SOLIDWORKS PART (.sldprt)
format: sldprt  version: not decoded by parser v0  size: 606,208 bytes
history: native  units: mm
features: sketch x494, extrude x1 + 10 further entries (+10 scaffold rows collapsed; 88 parser-record rows omitted)
feature tree (603):
  "Annotations"  RD1=95.25mm RD2=113.058536mm RD3=120.65mm RD4=130.291107mm RD6=10.3124mm RD5=12.7mm RD7=12.7mm RD8=12.7mm RD9=12.7mm RD10=12.7mm RD11=10.3124mm RD12=10.3124mm RD13=14.199032mm
  scaffold x10  (default folders/planes/origin — collapsed)
  sketch  "Sketch2"  dims[c1.D1=6.35mm c1.D2=6.35mm c1.D3=3.175mm c1.D4=3.175mm c2.D1=2.54mm c2.D2=2.54mm c2.D3=1.27mm c2.D4=1.27mm c3.D2=2.54mm c3.D3=2.54mm c3.D1=2.54mm c3.D5=2.54mm c3.D6=2.54mm c4.D1=2.54mm c4.D7=2.54mm c5.D1=2.54mm c5.D5=2.54mm c5.D2=2.54mm c5.D3=2.54mm c5.D6=~1.365496mm c6.D1=304.8mm c7.D1=~44.215175deg c8.D1=~862.162868mm c9.D1=~23.628086mm c10.D1=~757.905383mm c11.D1=~6.290207mm c11.D6=~14.447018mm c12.D1=6.35mm c12.D2=6.35mm c13.D1=3.048mm c13.D2=3.048mm c14.D1=1.524mm c14.D2=1.524mm c15.D1=6.35mm c15.D2=6.35mm c16.D1=10.16mm c16.D2=10.16mm c16.D3=7.62mm c16.D4=7.62mm c16.D5=8.89mm c16.D6=8.89mm c17.D1=8.89mm c17.D2=6.35mm c17.D3=6.35mm c18.D1=2.54mm c18.D2=2.54mm c19.D1=2.54mm c19.D2=2.54mm c19.D4=1.27mm c19.D5=1.27mm c19.D3=4.572mm c20.D5=4.572mm c20.D3=4.572mm c21.D5=4.572mm c21.D3=2.54mm c22.D5=2.54mm c22.D6=2.54mm c22.D3=1.27mm c23.D5=16.51mm c23.D6=1.27mm c23.D7=1.27mm c23.D8=10.16mm c23.D9=2.54mm c24.D8=5.08mm c24.D9=5.08mm c24.D5=5.08mm c24.D6=5.08mm c25.D8=1.905mm c25.D9=1.905mm c25.D6=1.905mm c26.D8=1.905mm c26.D6=5.08mm c27.D8=1.905mm c27.D9=1.905mm]
  extrude  "Extrude3"  Depth=6.35mm RestraintType=1
  sketch  "Value"
  sketch  "cosRestraintComp:1"
  sketch  "cosRestraintComp:2"
  sketch  "cosRestraintComp:3"
  sketch  "cosRestraintComp:4"
  sketch  "cosRestraintComp:5"
  sketch  "cosRestraintComp:6"
  sketch  "Unit"
  sketch  "AnalysisType"
  sketch  "MeshType"
  sketch  "cosRestraintCompCheck1"
  sketch  "cosRestraintCompCheck2"
  sketch  "cosRestraintCompCheck3"
  sketch  "cosRestraintCompCheck4"
  sketch  "cosRestraintCompCheck5"
  sketch  "cosRestraintCompCheck6"
  sketch  "cosRestraintRefPlaneSet"
  sketch  "cosRestraintRefPlaneOrigin1"
  sketch  "cosRestraintRefPlaneOrigin2"
  sketch  "cosRestraintRefPlaneOrigin3"
  sketch  "cosRestraintRefPlaneXDir1"
  sketch  "cosRestraintRefPlaneXDir2"
  sketch  "cosRestraintRefPlaneXDir3"
  sketch  "cosRestraintRefPlaneNormal1"
  sketch  "cosRestraintRefPlaneNormal2"
  sketch  "cosRestraintRefPlaneNormal3"
  sketch  "cosRestraintCoordSystemType"
  sketch  "cosRestraintFaceTypeMask"  dims[cosFMVItemName=0.0deg cosLBCSymbolColor=0.0deg]
  sketch  "cosLBCState"
  sketch  "RestraintType"
  sketch  "Value"
  sketch  "cosRestraintComp:1"
  sketch  "cosRestraintComp:2"
  sketch  "cosRestraintComp:3"
  sketch  "cosRestraintComp:4"
  sketch  "cosRestraintComp:5"
  sketch  "cosRestraintComp:6"
  sketch  "Unit"
  sketch  "AnalysisType"
  sketch  "MeshType"
  sketch  "cosRestraintCompCheck1"
  sketch  "cosRestraintCompCheck2"
  sketch  "cosRestraintCompCheck3"
  sketch  "cosRestraintCompCheck4"
  sketch  "cosRestraintCompCheck5"
  sketch  "cosRestraintCompCheck6"
  sketch  "cosRestraintRefPlaneSet"
  sketch  "cosRestraintRefPlaneOrigin1"
  sketch  "cosRestraintRefPlaneOrigin2"
  sketch  "cosRestraintRefPlaneOrigin3"
  sketch  "cosRestraintRefPlaneXDir1"
  sketch  "cosRestraintRefPlaneXDir2"
  sketch  "cosRestraintRefPlaneXDir3"
  sketch  "cosRestraintRefPlaneNormal1"
  sketch  "cosRestraintRefPlaneNormal2"
  sketch  "cosRestraintRefPlaneNormal3"  dims[cosRestraintRefPlaneName=0.0deg]
  sketch  "cosRestraintCoordSystemType"
  sketch  "cosRestraintFaceTypeMask"  dims[cosFMVItemName=0.0deg cosLBCSymbolColor=0.0deg]
  sketch  "cosLBCState"
  "freq:Restraint-2"
  sketch  "RestraintType"
  sketch  "Value"
  sketch  "cosRestraintComp:1"
  sketch  "cosRestraintComp:2"
  sketch  "cosRestraintComp:3"
  sketch  "cosRestraintComp:4"
  sketch  "cosRestraintComp:5"
  sketch  "cosRestraintComp:6"
  sketch  "Unit"
  sketch  "AnalysisType"
  sketch  "MeshType"
  sketch  "cosRestraintCompCheck1"
  sketch  "cosRestraintCompCheck2"
  sketch  "cosRestraintCompCheck3"
  sketch  "cosRestraintCompCheck4"
  sketch  "cosRestraintCompCheck5"
  sketch  "cosRestraintCompCheck6"
  sketch  "cosRestraintRefPlaneSet"
  sketch  "cosRestraintRefPlaneOrigin1"
  sketch  "cosRestraintRefPlaneOrigin2"
  sketch  "cosRestraintRefPlaneOrigin3"
  sketch  "cosRestraintRefPlaneXDir1"
  sketch  "cosRestraintRefPlaneXDir2"
  sketch  "cosRestraintRefPlaneXDir3"
  sketch  "cosRestraintRefPlaneNormal1"
  sketch  "cosRestraintRefPlaneNormal2"
  sketch  "cosRestraintRefPlaneNormal3"  dims[cosRestraintRefPlaneName=0.0deg]
  sketch  "cosRestraintCoordSystemType"
  sketch  "cosRestraintFaceTypeMask"  dims[cosFMVItemName=0.0deg cosLBCSymbolColor=0.0deg]
  sketch  "cosLBCState"
  "freq:Force-1"
  sketch  "cosForceComp:1"
  sketch  "cosForceComp:2"
  sketch  "cosForceComp:3"
  sketch  "cosForceComp:4"
  sketch  "cosForceComp:5"
  sketch  "cosForceComp:6"
  sketch  "cosForceTorqueNF"
  sketch  "cosForceCompCheck1"
  sketch  "cosForceCompCheck2"
  sketch  "cosForceCompCheck3"
  sketch  "cosForceCompCheck4"
  sketch  "cosForceCompCheck5"
  sketch  "cosForceCompCheck6"
  sketch  "Unit"
  sketch  "AnalysisType"
  sketch  "MeshType"
  sketch  "cosForceRefPlaneSet"
  sketch  "cosForceRefPlaneOrigin1"
  sketch  "cosForceRefPlaneOrigin2"
  sketch  "cosForceRefPlaneOrigin3"
  sketch  "cosForceRefPlaneXDir1"
  sketch  "cosForceRefPlaneXDir2"
  sketch  "cosForceRefPlaneXDir3"
  sketch  "cosForceRefPlaneNormal1"
  sketch  "cosForceRefPlaneNormal2"
  sketch  "cosForceRefPlaneNormal3"  dims[cosForceRefPlaneName=0.0deg]
  sketch  "cosForceCoordSystemType"
  sketch  "cosForceType"  dims[cosFMVItemName=0.0deg]
  sketch  "cosDistributionType"  dims[cosDistributionCoordSysName=0.0deg]
  sketch  "cosDistributionCoef1"
  sketch  "cosDistributionCoef2"
  sketch  "cosDistributionCoef3"
  sketch  "cosDistributionCoef4"
  sketch  "cosDistributionCoef5"
  sketch  "cosDistributionCoef6"  dims[cosLBCSymbolColor=0.0deg]
  sketch  "cosLBCState"  dims[cosForce7=0.0]
  sketch  "cosForceComp:1"
  sketch  "cosForceComp:2"
  sketch  "cosForceComp:3"
  sketch  "cosForceComp:4"
  sketch  "cosForceComp:5"
  sketch  "cosForceComp:6"
  sketch  "cosForceTorqueNF"
  sketch  "cosForceCompCheck1"
  sketch  "cosForceCompCheck2"
  sketch  "cosForceCompCheck3"
  sketch  "cosForceCompCheck4"
  sketch  "cosForceCompCheck5"
  sketch  "cosForceCompCheck6"
  sketch  "Unit"
  sketch  "AnalysisType"
  sketch  "MeshType"
  sketch  "cosForceRefPlaneSet"
  sketch  "cosForceRefPlaneOrigin1"
  sketch  "cosForceRefPlaneOrigin2"
  sketch  "cosForceRefPlaneOrigin3"
  sketch  "cosForceRefPlaneXDir1"
  sketch  "cosForceRefPlaneXDir2"
  sketch  "cosForceRefPlaneXDir3"
  sketch  "cosForceRefPlaneNormal1"
  sketch  "cosForceRefPlaneNormal2"
  sketch  "cosForceRefPlaneNormal3"  dims[cosForceRefPlaneName=0.0deg]
  sketch  "cosForceCoordSystemType"
  sketch  "cosForceType"  dims[cosFMVItemName=0.0deg]
  sketch  "cosDistributionType"  dims[cosDistributionCoordSysName=0.0deg]
  sketch  "cosDistributionCoef1"
  sketch  "cosDistributionCoef2"
  sketch  "cosDistributionCoef3"
  sketch  "cosDistributionCoef4"
  sketch  "cosDistributionCoef5"
  sketch  "cosDistributionCoef6"  dims[cosLBCSymbolColor=0.0deg]
  sketch  "cosLBCState"
  "freq:Force-2"
  sketch  "cosForceComp:1"
  sketch  "cosForceComp:2"
  sketch  "cosForceComp:3"
  sketch  "cosForceComp:4"
  sketch  "cosForceComp:5"
  sketch  "cosForceComp:6"
  sketch  "cosForceTorqueNF"
  sketch  "cosForceCompCheck1"
  sketch  "cosForceCompCheck2"
  sketch  "cosForceCompCheck3"
  sketch  "cosForceCompCheck4"
  sketch  "cosForceCompCheck5"
  sketch  "cosForceCompCheck6"
  sketch  "Unit"
  sketch  "AnalysisType"
  sketch  "MeshType"
  sketch  "cosForceRefPlaneSet"
  sketch  "cosForceRefPlaneOrigin1"
  sketch  "cosForceRefPlaneOrigin2"
  sketch  "cosForceRefPlaneOrigin3"
  sketch  "cosForceRefPlaneXDir1"
  sketch  "cosForceRefPlaneXDir2"
  sketch  "cosForceRefPlaneXDir3"
  sketch  "cosForceRefPlaneNormal1"
  sketch  "cosForceRefPlaneNormal2"
  sketch  "cosForceRefPlaneNormal3"  dims[cosForceRefPlaneName=0.0deg]
  sketch  "cosForceCoordSystemType"
  sketch  "cosForceType"  dims[cosFMVItemName=0.0deg]
  sketch  "cosDistributionType"  dims[cosDistributionCoordSysName=0.0deg]
  sketch  "cosDistributionCoef1"
  sketch  "cosDistributionCoef2"
  sketch  "cosDistributionCoef3"
  sketch  "cosDistributionCoef4"
  sketch  "cosDistributionCoef5"
  sketch  "cosDistributionCoef6"  dims[cosLBCSymbolColor=0.0deg]
  sketch  "cosLBCState"
  "static:Restraint-3"
  sketch  "RestraintType"
  sketch  "Value"
  sketch  "cosRestraintComp:1"
  sketch  "cosRestraintComp:2"
  sketch  "cosRestraintComp:3"
  sketch  "cosRestraintComp:4"
  sketch  "cosRestraintComp:5"
  sketch  "cosRestraintComp:6"
  sketch  "Unit"
  sketch  "AnalysisType"
  sketch  "MeshType"
  sketch  "cosRestraintCompCheck1"
  sketch  "cosRestraintCompCheck2"
  sketch  "cosRestraintCompCheck3"
  sketch  "cosRestraintCompCheck4"
  sketch  "cosRestraintCompCheck5"
  sketch  "cosRestraintCompCheck6"
  sketch  "cosRestraintRefPlaneSet"
  sketch  "cosRestraintRefPlaneOrigin1"
  sketch  "cosRestraintRefPlaneOrigin2"
  sketch  "cosRestraintRefPlaneOrigin3"
  sketch  "cosRestraintRefPlaneXDir1"
  sketch  "cosRestraintRefPlaneXDir2"
  sketch  "cosRestraintRefPlaneXDir3"
  sketch  "cosRestraintRefPlaneNormal1"
  sketch  "cosRestraintRefPlaneNormal2"
  sketch  "cosRestraintRefPlaneNormal3"  dims[cosRestraintRefPlaneName=0.0deg]
  sketch  "cosRestraintCoordSystemType"
  sketch  "cosRestraintFaceTypeMask"  dims[cosFMVItemName=0.0deg cosLBCSymbolColor=0.0deg]
  sketch  "cosLBCState"
  "static:Restraint-4"
  sketch  "RestraintType"
  sketch  "Value"
  sketch  "cosRestraintComp:1"
  sketch  "cosRestraintComp:2"
  sketch  "cosRestraintComp:3"
  sketch  "cosRestraintComp:4"
  sketch  "cosRestraintComp:5"
  sketch  "cosRestraintComp:6"
  sketch  "Unit"
  sketch  "AnalysisType"
  sketch  "MeshType"
  sketch  "cosRestraintCompCheck1"
  sketch  "cosRestraintCompCheck2"
  sketch  "cosRestraintCompCheck3"
  sketch  "cosRestraintCompCheck4"
  sketch  "cosRestraintCompCheck5"
  sketch  "cosRestraintCompCheck6"
  sketch  "cosRestraintRefPlaneSet"
  sketch  "cosRestraintRefPlaneOrigin1"
  sketch  "cosRestraintRefPlaneOrigin2"
  sketch  "cosRestraintRefPlaneOrigin3"
  sketch  "cosRestraintRefPlaneXDir1"
  sketch  "cosRestraintRefPlaneXDir2"
  sketch  "cosRestraintRefPlaneXDir3"
  sketch  "cosRestraintRefPlaneNormal1"
  sketch  "cosRestraintRefPlaneNormal2"
  sketch  "cosRestraintRefPlaneNormal3"  dims[cosRestraintRefPlaneName=0.0deg]
  sketch  "cosRestraintCoordSystemType"
  sketch  "cosRestraintFaceTypeMask"  dims[cosFMVItemName=0.0deg cosLBCSymbolColor=0.0deg]
  sketch  "cosLBCState"
  "static:Force-3"
  sketch  "cosForceComp:1"
  sketch  "cosForceComp:2"
  sketch  "cosForceComp:3"
  sketch  "cosForceComp:4"
  sketch  "cosForceComp:5"
  sketch  "cosForceComp:6"
  sketch  "cosForceTorqueNF"
  sketch  "cosForceCompCheck1"
  sketch  "cosForceCompCheck2"
  sketch  "cosForceCompCheck3"
  sketch  "cosForceCompCheck4"
  sketch  "cosForceCompCheck5"
  sketch  "cosForceCompCheck6"
  sketch  "Unit"
  sketch  "AnalysisType"
  sketch  "MeshType"
  sketch  "cosForceRefPlaneSet"
  sketch  "cosForceRefPlaneOrigin1"
  sketch  "cosForceRefPlaneOrigin2"
  sketch  "cosForceRefPlaneOrigin3"
  sketch  "cosForceRefPlaneXDir1"
  sketch  "cosForceRefPlaneXDir2"
  sketch  "cosForceRefPlaneXDir3"
  sketch  "cosForceRefPlaneNormal1"
  sketch  "cosForceRefPlaneNormal2"
  sketch  "cosForceRefPlaneNormal3"  dims[cosForceRefPlaneName=0.0deg]
  sketch  "cosForceCoordSystemType"
  sketch  "cosForceType"  dims[cosFMVItemName=0.0deg]
  sketch  "cosDistributionType"  dims[cosDistributionCoordSysName=0.0deg]
  sketch  "cosDistributionCoef1"
  sketch  "cosDistributionCoef2"
  sketch  "cosDistributionCoef3"
  sketch  "cosDistributionCoef4"
  sketch  "cosDistributionCoef5"
  sketch  "cosDistributionCoef6"  dims[cosLBCSymbolColor=0.0deg]
  sketch  "cosLBCState"
  "static:Force-4"
  sketch  "cosForceComp:1"
  sketch  "cosForceComp:2"
  sketch  "cosForceComp:3"
  sketch  "cosForceComp:4"
  sketch  "cosForceComp:5"
  sketch  "cosForceComp:6"
  sketch  "cosForceTorqueNF"
  sketch  "cosForceCompCheck1"
  sketch  "cosForceCompCheck2"
  sketch  "cosForceCompCheck3"
  sketch  "cosForceCompCheck4"
  sketch  "cosForceCompCheck5"
  sketch  "cosForceCompCheck6"
  sketch  "Unit"
  sketch  "AnalysisType"
  sketch  "MeshType"
  sketch  "cosForceRefPlaneSet"
  sketch  "cosForceRefPlaneOrigin1"
  sketch  "cosForceRefPlaneOrigin2"
  sketch  "cosForceRefPlaneOrigin3"
  sketch  "cosForceRefPlaneXDir1"
  sketch  "cosForceRefPlaneXDir2"
  sketch  "cosForceRefPlaneXDir3"
  sketch  "cosForceRefPlaneNormal1"
  sketch  "cosForceRefPlaneNormal2"
  sketch  "cosForceRefPlaneNormal3"  dims[cosForceRefPlaneName=0.0deg]
  sketch  "cosForceCoordSystemType"
  sketch  "cosForceType"  dims[cosFMVItemName=0.0deg]
  sketch  "cosDistributionType"  dims[cosDistributionCoordSysName=0.0deg]
  sketch  "cosDistributionCoef1"
  sketch  "cosDistributionCoef2"
  sketch  "cosDistributionCoef3"
  sketch  "cosDistributionCoef4"
  sketch  "cosDistributionCoef5"
  sketch  "cosDistributionCoef6"  dims[cosLBCSymbolColor=0.0deg]
  sketch  "cosLBCState"
  "static:Material-1"
  sketch  "cosMaterialEX"
  sketch  "cosMaterialNUXY"
  sketch  "cosMaterialGXY"
  sketch  "cosMaterialALPX"
  sketch  "cosMaterialDENS"
  sketch  "cosMaterialKX"
  sketch  "cosMaterialC"
  sketch  "Units"
  sketch  "AnalysisType"
  sketch  "MeshType"
  sketch  "cosMaterialSIGYLD"
  sketch  "cosMaterialSIGXT"
  sketch  "cosMaterialSIGXC"  dims[sMaterialSourceName=0.0deg sMaterialName=0.0deg cosFMVItemName=0.0deg cosMaterialName=0.0deg cosComponentName=0.0deg]
  sketch  "cosMaterialModel"
  sketch  "cosMaterialEY"
  sketch  "cosMaterialEZ"
  sketch  "cosMaterialNUXZ"
  sketch  "cosMaterialNUYZ"
  sketch  "cosMaterialGXZ"
  sketch  "cosMaterialGYZ"
  sketch  "cosMaterialALPY"
  sketch  "cosMaterialALPZ"
  sketch  "cosMaterialKY"
  sketch  "cosMaterialKZ"  dims[cosMaterialType=0.0deg cosMaterialLibFile=0.0deg cosMaterialRefPlaneName=0.0deg]
  sketch  "cosMaterialSource"  dims[cosMaterial7=0.0]
  sketch  "cosMaterialEX"
  sketch  "cosMaterialNUXY"
  sketch  "cosMaterialGXY"
  sketch  "cosMaterialALPX"
  sketch  "cosMaterialDENS"
  sketch  "cosMaterialKX"
  sketch  "cosMaterialC"
  sketch  "Units"
  sketch  "AnalysisType"
  sketch  "MeshType"
  sketch  "cosMaterialSIGYLD"
  sketch  "cosMaterialSIGXT"
  sketch  "cosMaterialSIGXC"  dims[sMaterialSourceName=0.0deg sMaterialName=0.0deg cosFMVItemName=0.0deg cosMaterialName=0.0deg cosComponentName=0.0deg]
  sketch  "cosMaterialModel"
  sketch  "cosMaterialEY"
  sketch  "cosMaterialEZ"
  sketch  "cosMaterialNUXZ"
  sketch  "cosMaterialNUYZ"
  sketch  "cosMaterialGXZ"
  sketch  "cosMaterialGYZ"
  sketch  "cosMaterialALPY"
  sketch  "cosMaterialALPZ"
  sketch  "cosMaterialKY"
  sketch  "cosMaterialKZ"  dims[cosMaterialType=0.0deg cosMaterialLibFile=0.0deg cosMaterialRefPlaneName=0.0deg]
  sketch  "cosMaterialSource"
  parser-record x88  (decoder bookkeeping rows leaked as tree rows — omitted from the tree; the rows remain in map.json)
  sketch  "faceID"  dims[cosFaceID=0.0]
  sketch  "faceID"
  sketch  "faceID"
  sketch  "faceID"
  sketch  "faceID"
  sketch  "faceID"
  sketch  "faceID"
  sketch  "faceID"
  sketch  "faceID"
  sketch  "faceID"
  sketch  "faceID"
  sketch  "faceID"
  sketch  "faceID"
  sketch  "faceID"
  sketch  "faceID"
  sketch  "faceID"
  sketch  "faceID"
  sketch  "faceID"
  sketch  "faceID"
  sketch  "faceID"
  sketch  "faceID"
  sketch  "faceID"
  sketch  "faceID"
  sketch  "faceID"
  sketch  "faceID"
  sketch  "faceID"
  sketch  "faceID"
  sketch  "faceID"
  sketch  "faceID"
  sketch  "faceID"
  sketch  "faceID"
  sketch  "faceID"
  sketch  "faceID"
  sketch  "faceID"
  sketch  "faceID"
  sketch  "faceID"
  sketch  "faceID"
  sketch  "faceID"
  sketch  "faceID"
  sketch  "faceID"
  sketch  "faceID"
  sketch  "faceID"
  sketch  "faceID"
  sketch  "faceID"
  sketch  "faceID"
  sketch  "faceID"
  sketch  "faceID"
  sketch  "faceID"
  sketch  "faceID"
  sketch  "faceID"
  sketch  "faceID"
  sketch  "faceID"
  sketch  "faceID"
  sketch  "faceID"
  sketch  "faceID"
  sketch  "faceID"
  sketch  "faceID"
  sketch  "faceID"
  sketch  "faceID"
  sketch  "faceID"
  sketch  "faceID"
  sketch  "faceID"
  sketch  "faceID"
  sketch  "faceID"
  sketch  "faceID"
  sketch  "faceID"
  sketch  "faceID"
  sketch  "faceID"
  sketch  "faceID"
  sketch  "faceID"
  sketch  "faceID"
  sketch  "faceID"
  sketch  "faceID"
  sketch  "faceID"
  sketch  "faceID"
  sketch  "faceID"
  sketch  "faceID"
  sketch  "faceID"
  sketch  "faceID"
  sketch  "faceID"
  sketch  "faceID"
  sketch  "faceID"
  sketch  "faceID"
  sketch  "faceID"
  sketch  "faceID"
  sketch  "faceID"
  sketch  "faceID"
  sketch  "faceID"
  sketch  "faceID"
  "freq:Material-1"
  sketch  "cosMaterialEX"
  sketch  "cosMaterialNUXY"
  sketch  "cosMaterialGXY"
  sketch  "cosMaterialALPX"
  sketch  "cosMaterialDENS"
  sketch  "cosMaterialKX"
  sketch  "cosMaterialC"
  sketch  "Units"
  sketch  "AnalysisType"
  sketch  "MeshType"
  sketch  "cosMaterialSIGYLD"
  sketch  "cosMaterialSIGXT"
  sketch  "cosMaterialSIGXC"  dims[sMaterialSourceName=0.0deg sMaterialName=0.0deg cosFMVItemName=0.0deg cosMaterialName=0.0deg cosComponentName=0.0deg]
  sketch  "cosMaterialModel"
  sketch  "cosMaterialEY"
  sketch  "cosMaterialEZ"
  sketch  "cosMaterialNUXZ"
  sketch  "cosMaterialNUYZ"
  sketch  "cosMaterialGXZ"
  sketch  "cosMaterialGYZ"
  sketch  "cosMaterialALPY"
  sketch  "cosMaterialALPZ"
  sketch  "cosMaterialKY"
  sketch  "cosMaterialKZ"  dims[cosMaterialType=0.0deg cosMaterialLibFile=0.0deg cosMaterialRefPlaneName=0.0deg]
  sketch  "cosMaterialSource"
decode coverage: 40 of 495 modeling features carry decoded parameters; 10 rows unclassified (native names shown)
note: ~ marks probable driven/reference dimensions
note: suppression state not decoded; provenance and decode notes live in map.json
